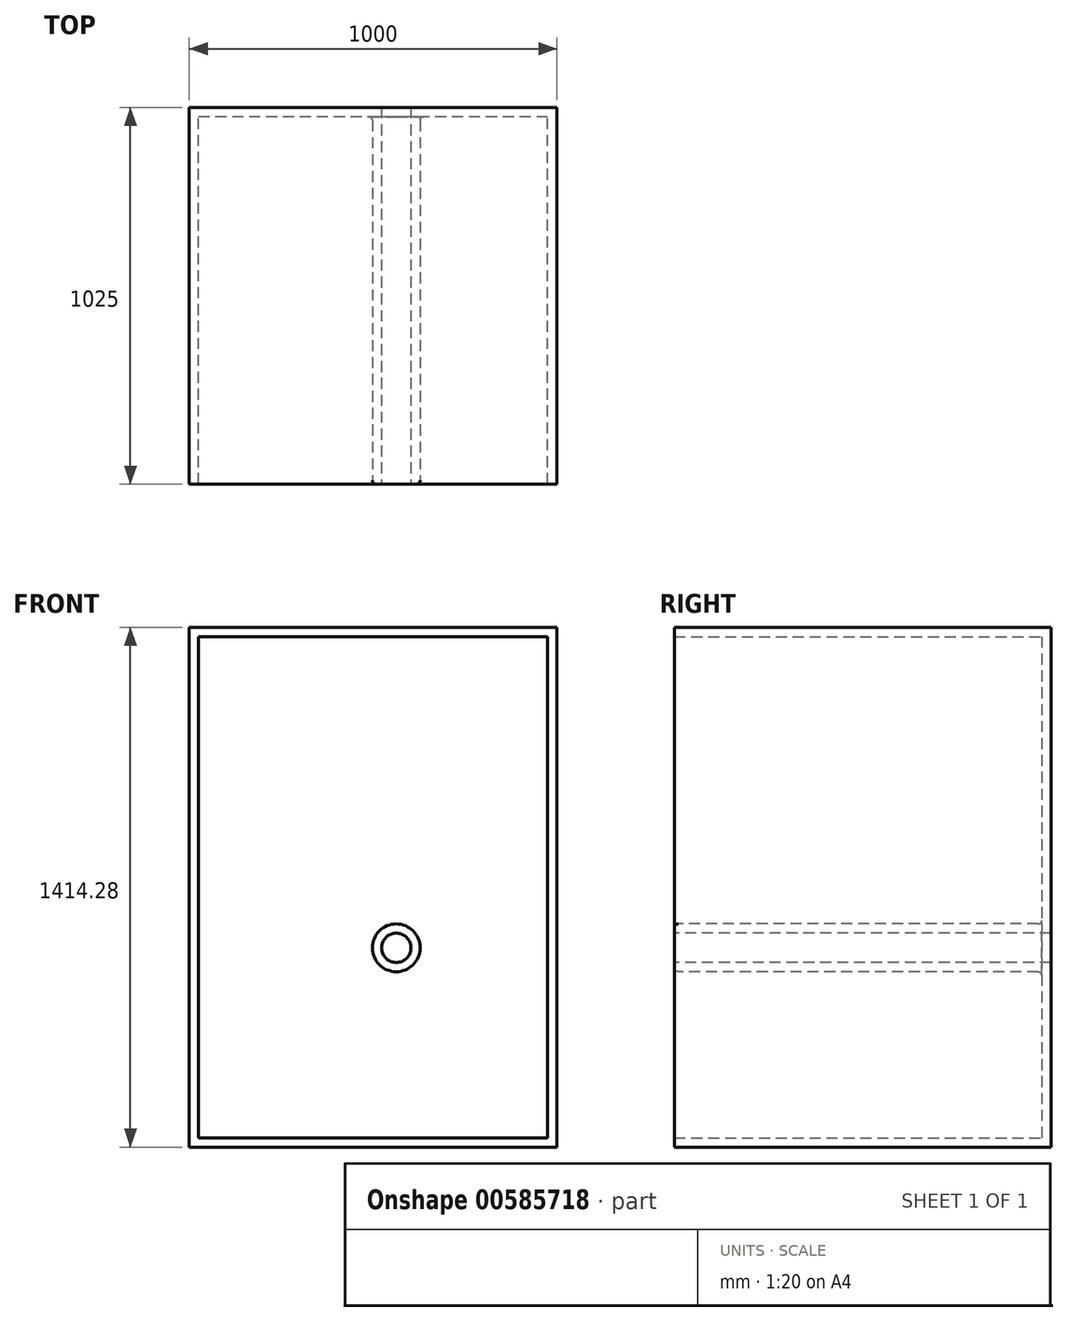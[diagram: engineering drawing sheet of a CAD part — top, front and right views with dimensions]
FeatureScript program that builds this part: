
annotation { "Feature Type Name" : "Feature", "Feature Type Description" : "" }
export const myFeature = defineFeature(function(context is Context, id is Id, definition is map)
    precondition{}
    {
        {
            var Q0;
            Q0=qCreatedBy(makeId("Front.planeOp"),FACE);
            var sketch = newSketch(context, id + "F0", { "sketchPlane" : qUnion([Q0])});
            skLineSegment(sketch, "E0.bottom", {"start": v(412.99, 537.51) * mm, "end": v(-587.01, 537.51) * mm});
            skLineSegment(sketch, "E0.top", {"start": v(412.99, -542.3) * mm, "end": v(-587.01, -542.3) * mm});
            skLineSegment(sketch, "E0.left", {"start": v(412.99, 537.51) * mm, "end": v(412.99, -542.3) * mm});
            skLineSegment(sketch, "E0.right", {"start": v(-587.01, 537.51) * mm, "end": v(-587.01, -542.3) * mm});
            skSolve(sketch);
        }
        {
            var Q0;
            Q0=makeQuery(id+"F0.imprint","IMPRINT",FACE,{"disambiguationData":[TD([[makeQuery(id+"F0.imprint","IMPRINT",EDGE,{"derivedFrom":sQuery(id+"F0.wireOp",EDGE,"E0.bottom")}),1.0]])]});
            extrude(context, id + "F1", {"entities" : qUnion([Q0]), "depth" : 1000 * mm, "offsetDistance" : 25 * mm});
        }
        {
            var Q0;
            Q0=makeQuery(id+"F1.opExtrude","CAP_FACE",FACE,{"disambiguationData":[OSD([sQuery(id+"F0.wireOp",EDGE,"E0.bottom"),sQuery(id+"F0.wireOp",EDGE,"E0.top"),sQuery(id+"F0.wireOp",EDGE,"E0.left"),sQuery(id+"F0.wireOp",EDGE,"E0.right")])],"isStart":false});
            var sketch = newSketch(context, id + "F2", { "sketchPlane" : qUnion([Q0])});
            skCircle(sketch, "E1", {"center": v(-23.86, 0) * mm, "radius": 40 * mm});
            skSolve(sketch);
        }
        {
            var Q0;
            Q0 = qSketchRegion(id + "F2", true);
            extrude(context, id + "F3", {"entities" : qUnion([Q0]), "operationType" : NewBodyOperationType.REMOVE, "oppositeDirection" : true, "depth" : 1463.37 * mm, "offsetDistance" : 25 * mm});
        }
        {
            var Q0;
            Q0=makeQuery(id+"F1.opExtrude","CAP_FACE",FACE,{"disambiguationData":[OSD([sQuery(id+"F0.wireOp",EDGE,"E0.bottom"),sQuery(id+"F0.wireOp",EDGE,"E0.top"),sQuery(id+"F0.wireOp",EDGE,"E0.left"),sQuery(id+"F0.wireOp",EDGE,"E0.right")])],"isStart":false});
            extrude(context, id + "F4", {"entities" : qUnion([Q0]), "operationType" : NewBodyOperationType.ADD, "depth" : 25 * mm, "offsetDistance" : 25 * mm});
        }
        {
            var Q0;
            {var subQ0=sQuery(id+"F0.wireOp",EDGE,"E0.bottom");Q0=makeQuery(id+"F4.boolean.opBoolean","MERGE",FACE,{"derivedFrom":[makeQuery(id+"F1.opExtrude","SWEPT_FACE",FACE,{"disambiguationData":[OSD([subQ0])]}),makeQuery(id+"F4.opExtrude","SWEPT_FACE",FACE,{"disambiguationData":[OSD([subQ0])]})]});}
            extrude(context, id + "F5", {"entities" : qUnion([Q0]), "operationType" : NewBodyOperationType.ADD, "depth" : 334.47 * mm, "offsetDistance" : 25 * mm});
        }
        {
            var Q0;
            {var subQ0=sQuery(id+"F0.wireOp",EDGE,"E0.bottom");Q0=makeQuery(id+"F5.boolean.opBoolean","MERGE",FACE,{"derivedFrom":[makeQuery(id+"F4.opExtrude","CAP_FACE",FACE,{"disambiguationData":[OSD([subQ0,sQuery(id+"F0.wireOp",EDGE,"E0.top"),sQuery(id+"F0.wireOp",EDGE,"E0.left"),sQuery(id+"F0.wireOp",EDGE,"E0.right")])],"isStart":false}),makeQuery(id+"F5.opExtrude","SWEPT_FACE",FACE,{"disambiguationData":[OSD([subQ0]),TDD([makeQuery(id+"F4.opExtrude","CAP_EDGE",EDGE,{"disambiguationData":[OSD([subQ0])],"isStart":false})])]})]});}
            shell(context, id + "F6", {"entities" : qUnion([Q0]), "thickness" : 25 * mm});
        }
        {
            var Q0;
            Q0=makeQuery(id+"F6.opShell","OFFSET_EDGE",EDGE,{"disambiguationData":[OSD([sQuery(id+"F0.wireOp",EDGE,"E0.bottom"),sQuery(id+"F0.wireOp",EDGE,"E0.top"),sQuery(id+"F0.wireOp",EDGE,"E0.left"),sQuery(id+"F0.wireOp",EDGE,"E0.right"),sQuery(id+"F2.wireOp",EDGE,"E1")])]});
            fillet(context, id + "F7", {"entities" : qUnion([Q0]), "radius" : 10 * mm, "tangentPropagation" : true, "allowEdgeOverflow" : false});
        }
    });
